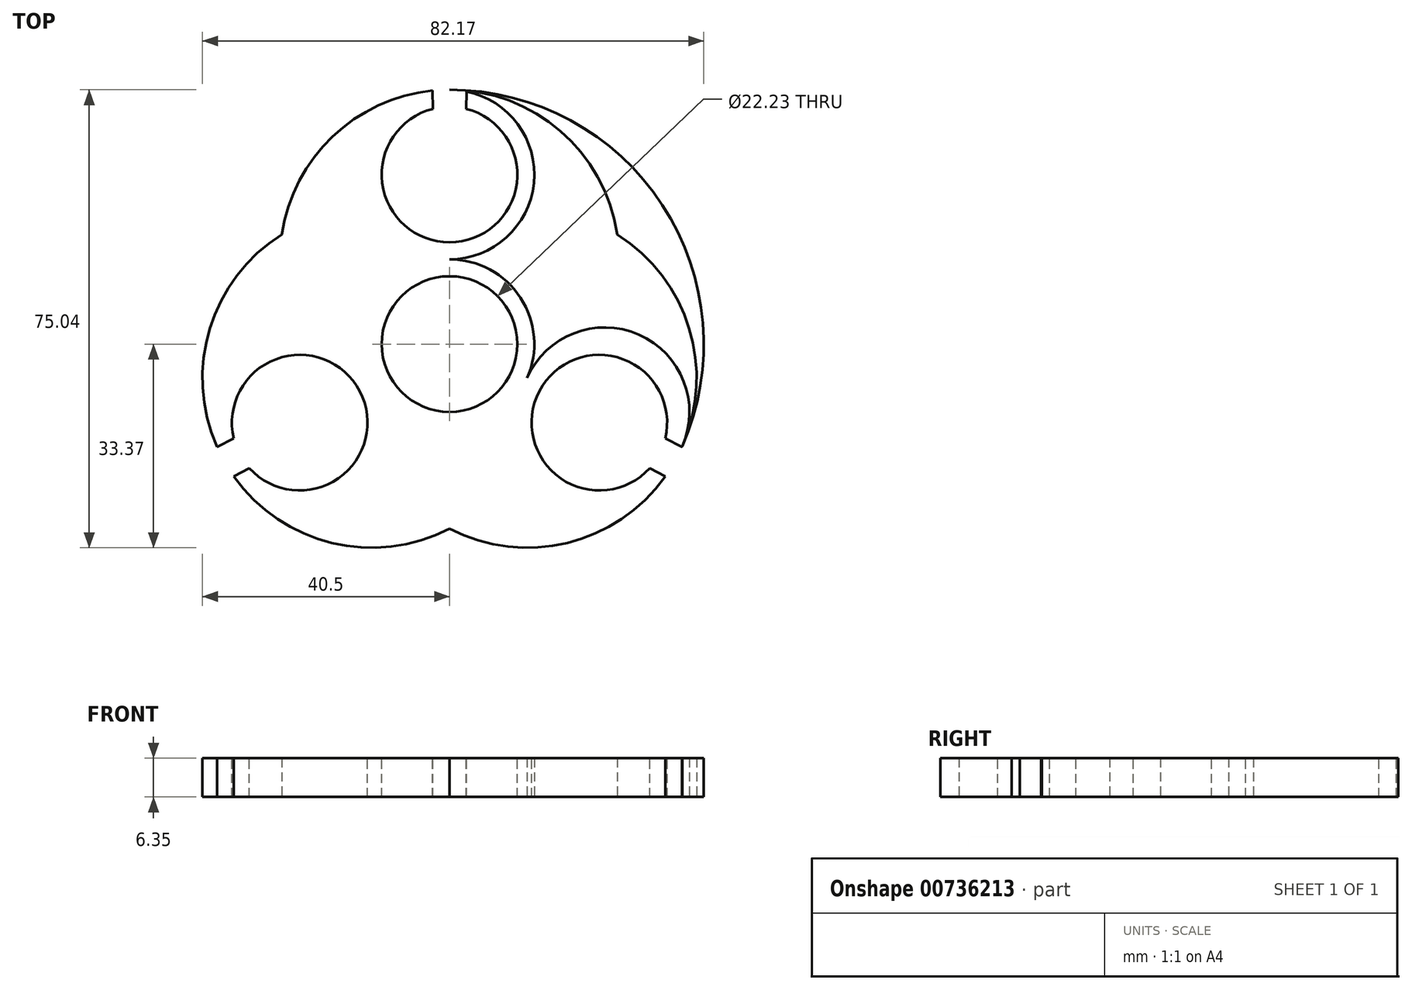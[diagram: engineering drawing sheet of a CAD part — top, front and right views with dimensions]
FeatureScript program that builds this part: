
annotation { "Feature Type Name" : "Feature", "Feature Type Description" : "" }
export const myFeature = defineFeature(function(context is Context, id is Id, definition is map)
    precondition{}
    {
        {
            var Q0;
            Q0=qCreatedBy(makeId("Top.planeOp"),FACE);
            var sketch = newSketch(context, id + "F0", { "sketchPlane" : qUnion([Q0])});
            skCircle(sketch, "E0", {"center": v(0, 0) * mm, "radius": 13.9 * mm});
            skCircle(sketch, "E1", {"center": v(0, 27.78) * mm, "radius": 13.9 * mm});
            skArc(sketch, "E2", {"start": v(0, 41.67) * mm, "mid": v(34.89, 22.79) * mm, "end": v(38.16, -16.75) * mm});
            skArc(sketch, "E3", {"start": v(38.16, -16.75) * mm, "mid": v(0, -41.67) * mm, "end": v(-38.16, -16.75) * mm});
            skArc(sketch, "E4", {"start": v(-38.16, -16.75) * mm, "mid": v(-34.89, 22.79) * mm, "end": v(0, 41.67) * mm});
            skCircle(sketch, "E5", {"center": v(25.44, -11.17) * mm, "radius": 13.9 * mm});
            skCircle(sketch, "E6", {"center": v(-25.44, -11.17) * mm, "radius": 13.9 * mm});
            skArc(sketch, "E7", {"start": v(0, 41.67) * mm, "mid": v(18.15, 34.92) * mm, "end": v(27.48, 17.95) * mm});
            skArc(sketch, "E8", {"start": v(0, 41.67) * mm, "mid": v(-18.15, 34.92) * mm, "end": v(-27.48, 17.95) * mm});
            skArc(sketch, "E9", {"start": v(-38.16, -16.75) * mm, "mid": v(-39.27, 2.58) * mm, "end": v(-27.48, 17.95) * mm});
            skArc(sketch, "E10", {"start": v(-38.16, -16.75) * mm, "mid": v(-22, -31.77) * mm, "end": v(0, -30.28) * mm});
            skArc(sketch, "E11", {"start": v(0, -30.28) * mm, "mid": v(22, -31.77) * mm, "end": v(38.16, -16.75) * mm});
            skArc(sketch, "E12", {"start": v(38.16, -16.75) * mm, "mid": v(39.27, 2.58) * mm, "end": v(27.48, 17.95) * mm});
            skSolve(sketch);
        }
        {
            var Q0;
            {var subQ0=sQuery(id+"F0.wireOp",EDGE,"E5");var subQ2=makeQuery(id+"F0.imprint","INTERSECT",VERTEX,{"derivedFrom":[sQuery(id+"F0.wireOp",EDGE,"E0"),subQ0]});Q0=makeQuery(id+"F0.imprint","IMPRINT",FACE,{"disambiguationData":[TD([[makeQuery(id+"F0.imprint","IMPRINT",EDGE,{"disambiguationData":[TD([[subQ2,-1.0]])],"derivedFrom":subQ0}),1.0]])]});}
            var Q1;
            {var subQ0=sQuery(id+"F0.wireOp",EDGE,"E8");Q1=makeQuery(id+"F0.imprint","IMPRINT",FACE,{"disambiguationData":[TD([[makeQuery(id+"F0.imprint","IMPRINT",EDGE,{"derivedFrom":subQ0}),1.0]])]});}
            var Q2;
            {var subQ0=sQuery(id+"F0.wireOp",EDGE,"E10");Q2=makeQuery(id+"F0.imprint","IMPRINT",FACE,{"disambiguationData":[TD([[makeQuery(id+"F0.imprint","IMPRINT",EDGE,{"derivedFrom":subQ0}),1.0]])]});}
            var Q3;
            {var subQ5=sQuery(id+"F0.wireOp",EDGE,"E7");Q3=makeQuery(id+"F0.imprint","IMPRINT",FACE,{"disambiguationData":[TD([[makeQuery(id+"F0.imprint","IMPRINT",EDGE,{"derivedFrom":subQ5}),-1.0]])]});}
            var Q4;
            {var subQ0=sQuery(id+"F0.wireOp",EDGE,"E6");var subQ2=makeQuery(id+"F0.imprint","INTERSECT",VERTEX,{"derivedFrom":[sQuery(id+"F0.wireOp",EDGE,"E0"),subQ0]});Q4=makeQuery(id+"F0.imprint","IMPRINT",FACE,{"disambiguationData":[TD([[makeQuery(id+"F0.imprint","IMPRINT",EDGE,{"disambiguationData":[TD([[subQ2,-1.0]])],"derivedFrom":subQ0}),1.0]])]});}
            var Q5;
            {var subQ0=sQuery(id+"F0.wireOp",EDGE,"E0");var subQ1=makeQuery(id+"F0.imprint","INTERSECT",VERTEX,{"derivedFrom":[subQ0,sQuery(id+"F0.wireOp",EDGE,"E6")]});Q5=makeQuery(id+"F0.imprint","IMPRINT",FACE,{"disambiguationData":[TD([[makeQuery(id+"F0.imprint","IMPRINT",EDGE,{"disambiguationData":[TD([[subQ1,1.0]])],"derivedFrom":subQ0}),1.0]])]});}
            var Q6;
            {var subQ0=sQuery(id+"F0.wireOp",EDGE,"E1");var subQ2=makeQuery(id+"F0.imprint","INTERSECT",VERTEX,{"derivedFrom":[sQuery(id+"F0.wireOp",EDGE,"E0"),subQ0]});Q6=makeQuery(id+"F0.imprint","IMPRINT",FACE,{"disambiguationData":[TD([[makeQuery(id+"F0.imprint","IMPRINT",EDGE,{"disambiguationData":[TD([[subQ2,1.0]])],"derivedFrom":subQ0}),1.0]])]});}
            extrude(context, id + "F1", {"entities" : qUnion([Q0, Q1, Q2, Q3, Q4, Q5, Q6]), "depth" : 6.35 * mm, "offsetDistance" : 25.4 * mm});
        }
        {
            var Q0;
            Q0=makeQuery(id+"F1.opExtrude","CAP_FACE",FACE,{"disambiguationData":[OSD([sQuery(id+"F0.wireOp",EDGE,"E7"),sQuery(id+"F0.wireOp",EDGE,"E8"),sQuery(id+"F0.wireOp",EDGE,"E9"),sQuery(id+"F0.wireOp",EDGE,"E10"),sQuery(id+"F0.wireOp",EDGE,"E11"),sQuery(id+"F0.wireOp",EDGE,"E12")])],"isStart":false});
            var sketch = newSketch(context, id + "F2", { "sketchPlane" : qUnion([Q0])});
            skCircle(sketch, "E13", {"center": v(0, 0) * mm, "radius": 11.11 * mm});
            skLineSegment(sketch, "E14", {"start": v(0, 41.67) * mm, "end": v(0, 27.78) * mm});
            skLineSegment(sketch, "E15", {"start": v(36.86, -19.34) * mm, "end": v(24.56, -12.88) * mm});
            skLineSegment(sketch, "E16", {"start": v(-36.86, -19.34) * mm, "end": v(-24.56, -12.88) * mm});
            skCircle(sketch, "E17", {"center": v(0, 27.78) * mm, "radius": 11.11 * mm});
            skCircle(sketch, "E18", {"center": v(-24.56, -12.88) * mm, "radius": 11.11 * mm});
            skCircle(sketch, "E19", {"center": v(24.56, -12.88) * mm, "radius": 11.11 * mm});
            skLineSegment(sketch, "E20", {"start": v(35.37, -15.44) * mm, "end": v(38.1, -16.86) * mm});
            skLineSegment(sketch, "E21", {"start": v(32.8, -20.33) * mm, "end": v(35.36, -21.68) * mm});
            skLineSegment(sketch, "E22", {"start": v(-38.1, -16.86) * mm, "end": v(-35.37, -15.44) * mm});
            skLineSegment(sketch, "E23", {"start": v(-35.36, -21.68) * mm, "end": v(-32.8, -20.33) * mm});
            skLineSegment(sketch, "E24", {"start": v(-2.76, 38.55) * mm, "end": v(-2.77, 41.53) * mm});
            skLineSegment(sketch, "E25", {"start": v(2.77, 41.53) * mm, "end": v(2.76, 38.55) * mm});
            skSolve(sketch);
        }
        {
            var Q0;
            Q0 = qSketchRegion(id + "F2", true);
            var Q1;
            {var subQ5=sQuery(id+"F2.wireOp",EDGE,"E24");Q1=makeQuery(id+"F2.imprint","IMPRINT",FACE,{"disambiguationData":[TD([[makeQuery(id+"F2.imprint","IMPRINT",EDGE,{"derivedFrom":subQ5}),-1.0]])]});}
            var Q2;
            {var subQ5=sQuery(id+"F2.wireOp",EDGE,"E25");Q2=makeQuery(id+"F2.imprint","IMPRINT",FACE,{"disambiguationData":[TD([[makeQuery(id+"F2.imprint","IMPRINT",EDGE,{"derivedFrom":subQ5}),-1.0]])]});}
            var Q3;
            {var subQ5=sQuery(id+"F2.wireOp",EDGE,"E21");Q3=makeQuery(id+"F2.imprint","IMPRINT",FACE,{"disambiguationData":[TD([[makeQuery(id+"F2.imprint","IMPRINT",EDGE,{"derivedFrom":subQ5}),1.0]])]});}
            var Q4;
            {var subQ5=sQuery(id+"F2.wireOp",EDGE,"E20");Q4=makeQuery(id+"F2.imprint","IMPRINT",FACE,{"disambiguationData":[TD([[makeQuery(id+"F2.imprint","IMPRINT",EDGE,{"derivedFrom":subQ5}),-1.0]])]});}
            var Q5;
            {var subQ5=sQuery(id+"F2.wireOp",EDGE,"E23");Q5=makeQuery(id+"F2.imprint","IMPRINT",FACE,{"disambiguationData":[TD([[makeQuery(id+"F2.imprint","IMPRINT",EDGE,{"derivedFrom":subQ5}),1.0]])]});}
            var Q6;
            {var subQ5=sQuery(id+"F2.wireOp",EDGE,"E22");Q6=makeQuery(id+"F2.imprint","IMPRINT",FACE,{"disambiguationData":[TD([[makeQuery(id+"F2.imprint","IMPRINT",EDGE,{"derivedFrom":subQ5}),-1.0]])]});}
            extrude(context, id + "F3", {"entities" : qUnion([Q0, Q1, Q2, Q3, Q4, Q5, Q6]), "operationType" : NewBodyOperationType.REMOVE, "oppositeDirection" : true, "depth" : 25.4 * mm, "offsetDistance" : 25.4 * mm});
        }
    });
